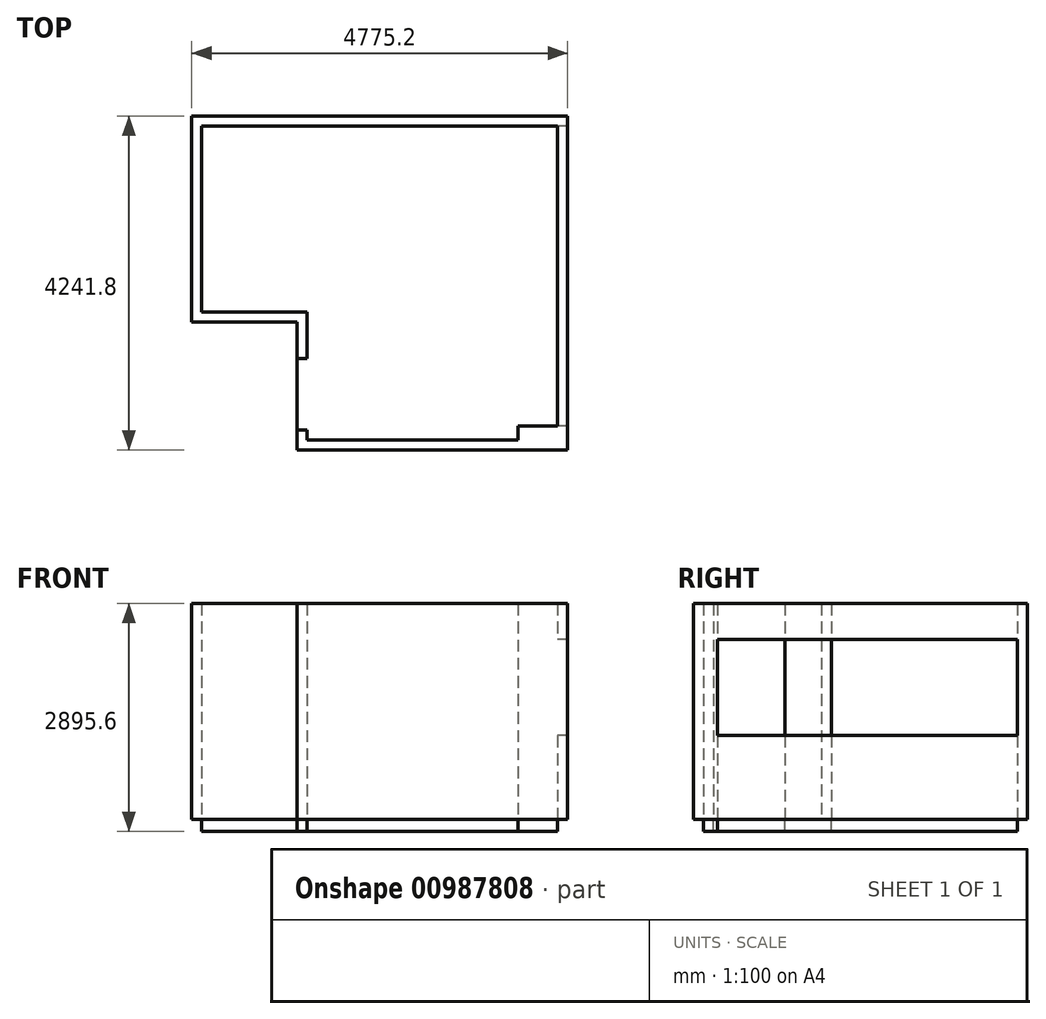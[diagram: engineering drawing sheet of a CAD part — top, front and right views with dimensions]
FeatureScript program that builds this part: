
annotation { "Feature Type Name" : "Feature", "Feature Type Description" : "" }
export const myFeature = defineFeature(function(context is Context, id is Id, definition is map)
    precondition{}
    {
        {
            var Q0;
            Q0=qCreatedBy(makeId("Top.planeOp"),FACE);
            var sketch = newSketch(context, id + "F0", { "sketchPlane" : qUnion([Q0])});
            skLineSegment(sketch, "E0.bottom", {"start": v(1339.85, 307.42) * mm, "end": v(4019.55, 307.42) * mm});
            skLineSegment(sketch, "E0.top", {"start": v(0, 4295.22) * mm, "end": v(4521.2, 4295.22) * mm});
            skLineSegment(sketch, "E0.left", {"start": v(0, 1933.02) * mm, "end": v(0, 4295.22) * mm});
            skLineSegment(sketch, "E0.right", {"start": v(4521.2, 485.22) * mm, "end": v(4521.2, 4295.22) * mm});
            skLineSegment(sketch, "E1", {"start": v(1339.85, 1933.02) * mm, "end": v(1339.85, 1339.3) * mm});
            skLineSegment(sketch, "E2.trimOffspring", {"start": v(1339.85, 1933.02) * mm, "end": v(0, 1933.02) * mm});
            skLineSegment(sketch, "E3.top", {"start": v(4521.2, 485.22) * mm, "end": v(4019.55, 485.22) * mm});
            skLineSegment(sketch, "E3.right", {"start": v(4019.55, 307.42) * mm, "end": v(4019.55, 485.22) * mm});
            skLineSegment(sketch, "E4", {"start": v(1212.85, 1339.3) * mm, "end": v(1339.85, 1339.3) * mm});
            skLineSegment(sketch, "E5.0", {"start": v(4648.2, 180.42) * mm, "end": v(4648.2, 4422.22) * mm});
            skLineSegment(sketch, "E6.0", {"start": v(-127, 1806.02) * mm, "end": v(-127, 4422.22) * mm});
            skLineSegment(sketch, "E7.0", {"start": v(-127, 4422.22) * mm, "end": v(4648.2, 4422.22) * mm});
            skLineSegment(sketch, "E8.0", {"start": v(1212.85, 180.42) * mm, "end": v(4648.2, 180.42) * mm});
            skLineSegment(sketch, "E9.0", {"start": v(1212.85, 1806.02) * mm, "end": v(-127, 1806.02) * mm});
            skLineSegment(sketch, "E10.0", {"start": v(1212.85, 1806.02) * mm, "end": v(1212.85, 1339.3) * mm});
            skLineSegment(sketch, "E11.trimOffspring", {"start": v(1339.85, 431.25) * mm, "end": v(1212.85, 431.25) * mm});
            skLineSegment(sketch, "E12.trimOffspring", {"start": v(1339.85, 431.25) * mm, "end": v(1339.85, 307.42) * mm});
            skLineSegment(sketch, "E13.trimOffspring", {"start": v(1212.85, 431.25) * mm, "end": v(1212.85, 180.42) * mm});
            skLineSegment(sketch, "E14", {"start": v(1339.85, 431.25) * mm, "end": v(1339.85, 1339.3) * mm});
            skLineSegment(sketch, "E15", {"start": v(1212.85, 431.25) * mm, "end": v(1212.85, 1339.3) * mm});
            skSolve(sketch);
        }
        {
            var Q0;
            Q0=makeQuery(id+"F0.imprint","IMPRINT",FACE,{"disambiguationData":[TD([[makeQuery(id+"F0.imprint","IMPRINT",EDGE,{"derivedFrom":sQuery(id+"F0.wireOp",EDGE,"E0.bottom")}),-1.0]])]});
            extrude(context, id + "F1", {"entities" : qUnion([Q0]), "depth" : 9 * 304.8 * mm, "offsetDistance" : 25.4 * mm});
        }
        {
            var Q0;
            Q0=makeQuery(id+"F1.opExtrude","SWEPT_FACE",FACE,{"disambiguationData":[OSD([sQuery(id+"F0.wireOp",EDGE,"E0.right")])]});
            var sketch = newSketch(context, id + "F2", { "sketchPlane" : qUnion([Q0])});
            skLineSegment(sketch, "E16.top", {"start": v(-4295.22, 1066.8) * mm, "end": v(-485.22, 1066.8) * mm});
            skLineSegment(sketch, "E16.left", {"start": v(-4295.22, 2286) * mm, "end": v(-4295.22, 1066.8) * mm});
            skLineSegment(sketch, "E16.right", {"start": v(-485.22, 2286) * mm, "end": v(-485.22, 1066.8) * mm});
            skLineSegment(sketch, "E17", {"start": v(-4295.22, 2286) * mm, "end": v(-485.22, 2286) * mm});
            skPoint(sketch, "E18.orphan", {"position": v(0, 2286) * mm});
            skSolve(sketch);
        }
        {
            var Q0;
            Q0=makeQuery(id+"F2.imprint","IMPRINT",FACE,{"disambiguationData":[TD([[makeQuery(id+"F2.imprint","IMPRINT",EDGE,{"derivedFrom":sQuery(id+"F2.wireOp",EDGE,"E16.top")}),1.0]])]});
            extrude(context, id + "F3", {"entities" : qUnion([Q0]), "operationType" : NewBodyOperationType.REMOVE, "endBound" : BoundingType.UP_TO_NEXT, "oppositeDirection" : true, "depth" : 25.4 * mm, "offsetDistance" : 25.4 * mm});
        }
        {
            var Q0;
            Q0=makeQuery(id+"F0.imprint","IMPRINT",FACE,{"disambiguationData":[TD([[makeQuery(id+"F0.imprint","IMPRINT",EDGE,{"derivedFrom":sQuery(id+"F0.wireOp",EDGE,"E0.bottom")}),1.0]])]});
            var Q1;
            Q1=makeQuery(id+"F0.imprint","IMPRINT",FACE,{"disambiguationData":[TD([[makeQuery(id+"F0.imprint","IMPRINT",EDGE,{"derivedFrom":sQuery(id+"F0.wireOp",EDGE,"E4")}),-1.0]])]});
            extrude(context, id + "F4", {"entities" : qUnion([Q0, Q1]), "operationType" : NewBodyOperationType.ADD, "oppositeDirection" : true, "depth" : 152.4 * mm, "offsetDistance" : 25.4 * mm});
        }
    });
